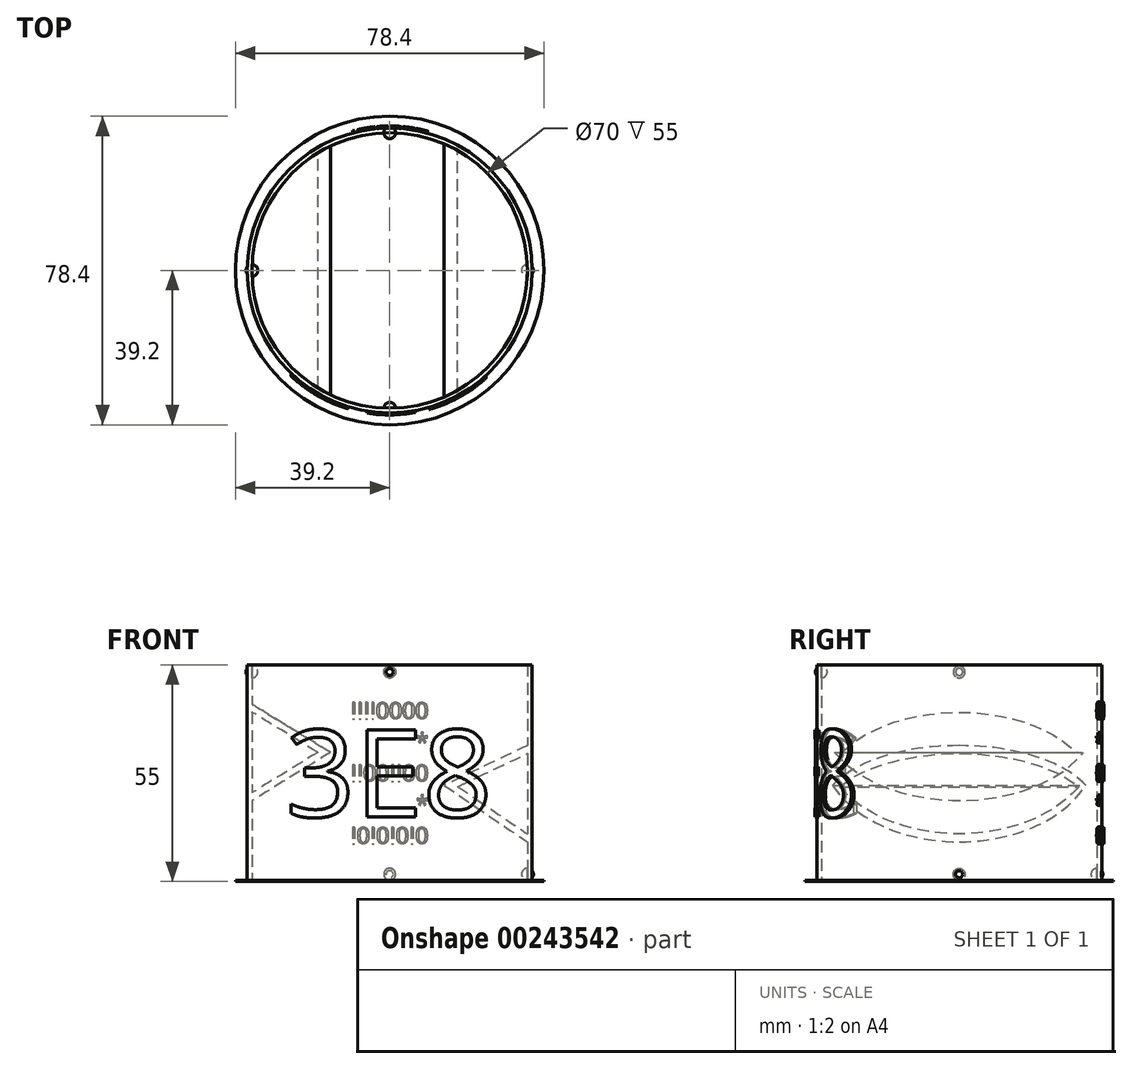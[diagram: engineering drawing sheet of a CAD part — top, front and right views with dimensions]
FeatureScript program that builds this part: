
annotation { "Feature Type Name" : "Feature", "Feature Type Description" : "" }
export const myFeature = defineFeature(function(context is Context, id is Id, definition is map)
    precondition{}
    {
        {
            var Q0;
            Q0=qCreatedBy(makeId("Top.planeOp"),FACE);
            var sketch = newSketch(context, id + "F0", { "sketchPlane" : qUnion([Q0])});
            skCircle(sketch, "E0", {"center": v(0, 0) * mm, "radius": 35 * mm});
            skCircle(sketch, "E1.0", {"center": v(0, 0) * mm, "radius": 36.2 * mm});
            skSolve(sketch);
        }
        {
            var Q0;
            Q0=qSketchRegion(id+"F0",true);
            extrude(context, id + "F1", {"entities" : qUnion([Q0]), "depth" : 55 * mm});
        }
        {
            var Q0;
            Q0=makeQuery(id+"F1.opExtrude","CAP_FACE",FACE,{"disambiguationData":[OSD([sQuery(id+"F0.wireOp",EDGE,"E0"),sQuery(id+"F0.wireOp",EDGE,"E1.0")])],"isStart":false});
            cPlane(context, id + "F2", {"entities" : qUnion([Q0]), "cplaneType" : CPlaneType.OFFSET, "offset" : 4 * mm, "width" : 150 * mm, "height" : 150 * mm});
        }
        {
            var Q0;
            Q0=makeQuery(id+"F1.opExtrude","CAP_FACE",FACE,{"disambiguationData":[OSD([sQuery(id+"F0.wireOp",EDGE,"E0"),sQuery(id+"F0.wireOp",EDGE,"E1.0")])],"isStart":true});
            cPlane(context, id + "F3", {"entities" : qUnion([Q0]), "cplaneType" : CPlaneType.OFFSET, "offset" : 4 * mm, "width" : 150 * mm, "height" : 150 * mm});
        }
        {
            var Q0;
            Q0=makeQuery(id+"F1.opExtrude","CAP_FACE",FACE,{"disambiguationData":[OSD([sQuery(id+"F0.wireOp",EDGE,"E0"),sQuery(id+"F0.wireOp",EDGE,"E1.0")])],"isStart":true});
            cPlane(context, id + "F4", {"entities" : qUnion([Q0]), "cplaneType" : CPlaneType.OFFSET, "offset" : 27.5 * mm, "oppositeDirection" : true, "width" : 150 * mm, "height" : 150 * mm});
        }
        {
            var Q0;
            Q0=qCreatedBy(id+"F2.planeOp",FACE);
            var sketch = newSketch(context, id + "F5", { "sketchPlane" : qUnion([Q0])});
            skCircle(sketch, "E2.0", {"center": v(0, 0) * mm, "radius": 36.2 * mm});
            skSolve(sketch);
        }
        {
            var Q0;
            Q0=makeQuery(id+"F1.opExtrude","CAP_FACE",FACE,{"disambiguationData":[OSD([sQuery(id+"F0.wireOp",EDGE,"E0"),sQuery(id+"F0.wireOp",EDGE,"E1.0")])],"isStart":false});
            extrude(context, id + "F6", {"entities" : qUnion([Q0]), "operationType" : NewBodyOperationType.ADD, "depth" : 2 * mm});
        }
        {
            var Q0;
            Q0=qCreatedBy(id+"F4.planeOp",FACE);
            var sketch = newSketch(context, id + "F7", { "sketchPlane" : qUnion([Q0])});
            skCircle(sketch, "E3.0", {"center": v(0, 0) * mm, "radius": 35 * mm});
            skSolve(sketch);
        }
        {
            var Q0;
            Q0=qSketchRegion(id+"F7",true);
            extrude(context, id + "F8", {"entities" : qUnion([Q0]), "operationType" : NewBodyOperationType.REMOVE, "oppositeDirection" : true, "depth" : 22 * mm, "hasSecondDirection" : true, "secondDirectionOppositeDirection" : false, "secondDirectionDepth" : 22 * mm});
        }
        {
            var Q0;
            Q0=qCreatedBy(makeId("Front.planeOp"),FACE);
            var sketch = newSketch(context, id + "F9", { "sketchPlane" : qUnion([Q0])});
            skLineSegment(sketch, "E4", {"start": v(-35, 0) * mm, "end": v(-35, 55) * mm, "construction": true});
            skLineSegment(sketch, "E5", {"start": v(35, 55) * mm, "end": v(35, 0) * mm, "construction": true});
            skLineSegment(sketch, "E6", {"start": v(-35, 55) * mm, "end": v(-35, 45) * mm, "construction": true});
            skLineSegment(sketch, "E7.0", {"start": v(-35, 55) * mm, "end": v(35, 55) * mm, "construction": true});
            skLineSegment(sketch, "E8", {"start": v(-35, 45) * mm, "end": v(-15, 32.75) * mm});
            skLineSegment(sketch, "E9", {"start": v(-15, 32.75) * mm, "end": v(-35, 20.5) * mm});
            skLineSegment(sketch, "E10", {"start": v(-35, 20.5) * mm, "end": v(-35, 22.5) * mm});
            skLineSegment(sketch, "E11", {"start": v(-35, 22.5) * mm, "end": v(-18.27, 32.75) * mm});
            skLineSegment(sketch, "E12", {"start": v(-18.27, 32.75) * mm, "end": v(-35, 43) * mm});
            skLineSegment(sketch, "E13", {"start": v(-35, 43) * mm, "end": v(-35, 45) * mm});
            skLineSegment(sketch, "E14", {"start": v(-15, 32.75) * mm, "end": v(-35, 32.75) * mm, "construction": true});
            skLineSegment(sketch, "E15", {"start": v(-35, 0) * mm, "end": v(35, 0) * mm, "construction": true});
            skLineSegment(sketch, "E16", {"start": v(35, 0) * mm, "end": v(35, 10) * mm, "construction": true});
            skLineSegment(sketch, "E17", {"start": v(35, 34.5) * mm, "end": v(13.83, 24.4) * mm});
            skLineSegment(sketch, "E18", {"start": v(13.83, 24.4) * mm, "end": v(35, 10) * mm});
            skLineSegment(sketch, "E19", {"start": v(35, 12) * mm, "end": v(17.29, 24.05) * mm});
            skLineSegment(sketch, "E20", {"start": v(17.29, 24.05) * mm, "end": v(35, 32.5) * mm});
            skLineSegment(sketch, "E21", {"start": v(35, 32.5) * mm, "end": v(35, 34.5) * mm});
            skLineSegment(sketch, "E22", {"start": v(35, 12) * mm, "end": v(35, 10) * mm});
            skLineSegment(sketch, "E23", {"start": v(-35, 27.5) * mm, "end": v(35, 27.5) * mm, "construction": true});
            skLineSegment(sketch, "E24", {"start": v(-35, 27.5) * mm, "end": v(-35, 22.5) * mm, "construction": true});
            skLineSegment(sketch, "E25", {"start": v(35, 32.5) * mm, "end": v(35, 27.5) * mm, "construction": true});
            skPoint(sketch, "E26", {"position": v(0, 27.5) * mm});
            skPoint(sketch, "E27", {"position": v(48.42, 25.24) * mm});
            skSolve(sketch);
        }
        {
            var Q0;
            Q0=qSketchRegion(id+"F9",true);
            extrude(context, id + "F10", {"entities" : qUnion([Q0]), "operationType" : NewBodyOperationType.ADD, "endBound" : BoundingType.UP_TO_NEXT, "depth" : 25 * mm, "hasSecondDirection" : true, "secondDirectionBound" : SecondDirectionBoundingType.UP_TO_NEXT, "secondDirectionOppositeDirection" : true, "secondDirectionDepth" : 25 * mm});
        }
        {
            var Q0;
            Q0=qCreatedBy(id+"F3.planeOp",FACE);
            var sketch = newSketch(context, id + "F11", { "sketchPlane" : qUnion([Q0])});
            skCircle(sketch, "E28.0", {"center": v(0, 0) * mm, "radius": 36.2 * mm});
            skSolve(sketch);
        }
        {
            var Q0;
            Q0=qSketchRegion(id+"F11",true);
            extrude(context, id + "F12", {"entities" : qUnion([Q0]), "operationType" : NewBodyOperationType.REMOVE, "oppositeDirection" : true, "depth" : 4 * mm});
        }
        {
            var Q0;
            Q0=makeQuery(id+"F5.imprint","IMPRINT",FACE,{"disambiguationData":[TD([[makeQuery(id+"F5.imprint","IMPRINT",EDGE,{"derivedFrom":sQuery(id+"F5.wireOp",EDGE,"E2.0")}),1.0]])]});
            extrude(context, id + "F13", {"entities" : qUnion([Q0]), "operationType" : NewBodyOperationType.REMOVE, "oppositeDirection" : true, "depth" : 4 * mm});
        }
        {
            var Q0;
            Q0=makeQuery(id+"F12.boolean.opBoolean","MERGE",FACE,{"derivedFrom":[makeQuery(id+"F1.opExtrude","CAP_FACE",FACE,{"disambiguationData":[OSD([sQuery(id+"F0.wireOp",EDGE,"E0"),sQuery(id+"F0.wireOp",EDGE,"E1.0")])],"isStart":true}),makeQuery(id+"F12.opExtrude","CAP_FACE",FACE,{"disambiguationData":[OSD([sQuery(id+"F11.wireOp",EDGE,"E28.0")])],"isStart":false})]});
            var sketch = newSketch(context, id + "F14", { "sketchPlane" : qUnion([Q0])});
            skCircle(sketch, "E29.0", {"center": v(0, 0) * mm, "radius": 36.2 * mm});
            skCircle(sketch, "E30.0", {"center": v(0, 0) * mm, "radius": 39.2 * mm});
            skSolve(sketch);
        }
        {
            var Q0;
            Q0=makeQuery(id+"F14.imprint","IMPRINT",FACE,{"disambiguationData":[TD([[makeQuery(id+"F14.imprint","IMPRINT",EDGE,{"derivedFrom":sQuery(id+"F14.wireOp",EDGE,"E29.0")}),1.0]])]});
            extrude(context, id + "F15", {"entities" : qUnion([Q0]), "operationType" : NewBodyOperationType.ADD, "oppositeDirection" : true, "depth" : .3 * mm});
        }
        {
            var Q0;
            Q0=qCreatedBy(makeId("Front.planeOp"),FACE);
            cPlane(context, id + "F16", {"entities" : qUnion([Q0]), "cplaneType" : CPlaneType.OFFSET, "offset" : 40 * mm, "width" : 150 * mm, "height" : 150 * mm});
        }
        {
            var Q0;
            Q0=qCreatedBy(id+"F16.planeOp",FACE);
            var sketch = newSketch(context, id + "F17", { "sketchPlane" : qUnion([Q0])});
            skLineSegment(sketch, "E31", {"start": v(0, 0) * mm, "end": v(0, 27.5) * mm, "construction": true});
            skText(sketch, "E32", { "text": "3E8", "fontName": "OpenSans-Regular.ttf"});
            const initialGuessF17  = {"E32": [-0.02646, 0.01638, 1, 0, 0.02224]};
            skSetInitialGuess(sketch, initialGuessF17);
            skSolve(sketch);
        }
        {
            var Q0;
            Q0=qSketchRegion(id+"F17",true);
            extrude(context, id + "F18", {"entities" : qUnion([Q0]), "operationType" : NewBodyOperationType.ADD, "endBound" : BoundingType.UP_TO_NEXT, "oppositeDirection" : true, "depth" : 25 * mm});
        }
        {
            var Q0;
            Q0=qCreatedBy(makeId("Front.planeOp"),FACE);
            cPlane(context, id + "F19", {"entities" : qUnion([Q0]), "cplaneType" : CPlaneType.OFFSET, "offset" : 40 * mm, "oppositeDirection" : true, "width" : 150 * mm, "height" : 150 * mm});
        }
        {
            var Q0;
            Q0=qCreatedBy(id+"F19.planeOp",FACE);
            var sketch = newSketch(context, id + "F20", { "sketchPlane" : qUnion([Q0])});
            skLineSegment(sketch, "E33.0", {"start": v(0, 0) * mm, "end": v(0, 27.5) * mm, "construction": true});
            skText(sketch, "E34", { "text": "IIII0000\n           *\nII00II00\n           *\nI0I0I0I0", "fontName": "OpenSans-Regular.ttf"});
            skLineSegment(sketch, "E35", {"start": v(0, 27.5) * mm, "end": v(0, 45.5) * mm, "construction": true});
            const initialGuessF20  = {"E34": [-0.01, 0.0413, 1, 0, 0.0042]};
            skSetInitialGuess(sketch, initialGuessF20);
            skSolve(sketch);
        }
        {
            var Q0;
            Q0=qSketchRegion(id+"F20",true);
            extrude(context, id + "F21", {"entities" : qUnion([Q0]), "operationType" : NewBodyOperationType.ADD, "endBound" : BoundingType.UP_TO_NEXT, "depth" : 25 * mm});
        }
        {
            var Q0;
            Q0=makeQuery(id+"F15.opExtrude","CAP_FACE",FACE,{"disambiguationData":[OSD([sQuery(id+"F14.wireOp",EDGE,"E29.0"),sQuery(id+"F14.wireOp",EDGE,"E30.0")])],"isStart":false});
            var sketch = newSketch(context, id + "F22", { "sketchPlane" : qUnion([Q0])});
            skCircle(sketch, "E36.0", {"center": v(0, 0) * mm, "radius": 36.2 * mm, "construction": true});
            skCircle(sketch, "E37.0", {"center": v(0, 0) * mm, "radius": 36.7 * mm});
            skCircle(sketch, "E38.0", {"center": v(0, 0) * mm, "radius": 56.7 * mm});
            skSolve(sketch);
        }
        {
            var Q0;
            Q0=makeQuery(id+"F22.imprint","IMPRINT",FACE,{"disambiguationData":[TD([[makeQuery(id+"F22.imprint","IMPRINT",EDGE,{"derivedFrom":sQuery(id+"F22.wireOp",EDGE,"E38.0")}),1.0]])]});
            var Q1;
            Q1=makeQuery(id+"F22.imprint","IMPRINT",FACE,{"disambiguationData":[TD([[makeQuery(id+"F22.imprint","IMPRINT",EDGE,{"derivedFrom":sQuery(id+"F22.wireOp",EDGE,"E37.0")}),-1.0]])]});
            extrude(context, id + "F23", {"entities" : qUnion([Q0, Q1]), "operationType" : NewBodyOperationType.REMOVE, "endBound" : BoundingType.THROUGH_ALL, "depth" : 25 * mm});
        }
        {
            var Q0;
            Q0=qCreatedBy(makeId("Front.planeOp"),FACE);
            var sketch = newSketch(context, id + "F24", { "sketchPlane" : qUnion([Q0])});
            skLineSegment(sketch, "E39", {"start": v(-35, 0) * mm, "end": v(-35, 55) * mm, "construction": true});
            skLineSegment(sketch, "E40", {"start": v(35, 55) * mm, "end": v(35, 0) * mm, "construction": true});
            skLineSegment(sketch, "E41", {"start": v(-35, 54.7) * mm, "end": v(-35, 55) * mm, "construction": true});
            skLineSegment(sketch, "E42", {"start": v(-35, 54.7) * mm, "end": v(-35, 51.7) * mm});
            skArc(sketch, "E43", {"start": v(-35, 51.7) * mm, "mid": v(-33.5, 53.2) * mm, "end": v(-35, 54.7) * mm});
            skPoint(sketch, "E44", {"position": v(35, 27.5) * mm});
            skPoint(sketch, "E45", {"position": v(-35, 27.5) * mm});
            skLineSegment(sketch, "E46", {"start": v(-35, 27.5) * mm, "end": v(35, 27.5) * mm, "construction": true});
            skLineSegment(sketch, "E47", {"start": v(0, 27.5) * mm, "end": v(0, 55) * mm, "construction": true});
            skArc(sketch, "E48.MirrorCS", {"start": v(35, 51.7) * mm, "mid": v(33.5, 53.2) * mm, "end": v(35, 54.7) * mm});
            skLineSegment(sketch, "E49.MirrorCS", {"start": v(35, 54.7) * mm, "end": v(35, 51.7) * mm});
            skArc(sketch, "E50.MirrorCS", {"start": v(35, 3.3) * mm, "mid": v(33.5, 1.8) * mm, "end": v(35, 0.3) * mm});
            skLineSegment(sketch, "E51.MirrorCS", {"start": v(35, 0.3) * mm, "end": v(35, 3.3) * mm});
            skArc(sketch, "E52.MirrorCS", {"start": v(-35, 3.3) * mm, "mid": v(-33.5, 1.8) * mm, "end": v(-35, 0.3) * mm});
            skLineSegment(sketch, "E53.MirrorCS", {"start": v(-35, 0.3) * mm, "end": v(-35, 3.3) * mm});
            skLineSegment(sketch, "E54", {"start": v(-35, 0) * mm, "end": v(35, 0) * mm, "construction": true});
            skSolve(sketch);
        }
        {
            var Q0;
            Q0=makeQuery(id+"F24.imprint","IMPRINT",FACE,{"disambiguationData":[TD([[makeQuery(id+"F24.imprint","IMPRINT",EDGE,{"derivedFrom":sQuery(id+"F24.wireOp",EDGE,"E42")}),1.0]])]});
            var Q1;
            Q1=makeQuery(id+"F24.imprint","IMPRINT",FACE,{"disambiguationData":[TD([[makeQuery(id+"F24.imprint","IMPRINT",EDGE,{"derivedFrom":sQuery(id+"F24.wireOp",EDGE,"E52.MirrorCS")}),-1.0]])]});
            var Q2;
            Q2=sQuery(id+"F24.wireOp",EDGE,"E39");
            revolve(context, id + "F25", {"operationType" : NewBodyOperationType.ADD, "entities" : qUnion([Q0, Q1]), "axis" : qUnion([Q2]), "revolveType" : RevolveType.FULL});
        }
        {
            var Q0;
            Q0=makeQuery(id+"F24.imprint","IMPRINT",FACE,{"disambiguationData":[TD([[makeQuery(id+"F24.imprint","IMPRINT",EDGE,{"derivedFrom":sQuery(id+"F24.wireOp",EDGE,"E48.MirrorCS")}),-1.0]])]});
            var Q1;
            Q1=makeQuery(id+"F24.imprint","IMPRINT",FACE,{"disambiguationData":[TD([[makeQuery(id+"F24.imprint","IMPRINT",EDGE,{"derivedFrom":sQuery(id+"F24.wireOp",EDGE,"E50.MirrorCS")}),1.0]])]});
            var Q2;
            Q2=sQuery(id+"F24.wireOp",EDGE,"E40");
            revolve(context, id + "F26", {"operationType" : NewBodyOperationType.ADD, "entities" : qUnion([Q0, Q1]), "axis" : qUnion([Q2]), "revolveType" : RevolveType.FULL});
        }
        {
            var Q0;
            Q0=qCreatedBy(makeId("Right.planeOp"),FACE);
            var sketch = newSketch(context, id + "F27", { "sketchPlane" : qUnion([Q0])});
            skLineSegment(sketch, "E55", {"start": v(-35, 0) * mm, "end": v(-35, 55) * mm, "construction": true});
            skLineSegment(sketch, "E56", {"start": v(35, 55) * mm, "end": v(35, 0) * mm, "construction": true});
            skLineSegment(sketch, "E57", {"start": v(-35, 54.7) * mm, "end": v(-35, 55) * mm, "construction": true});
            skLineSegment(sketch, "E58", {"start": v(-35, 54.7) * mm, "end": v(-35, 51.7) * mm});
            skArc(sketch, "E59", {"start": v(-35, 51.7) * mm, "mid": v(-33.5, 53.2) * mm, "end": v(-35, 54.7) * mm});
            skPoint(sketch, "E60", {"position": v(35, 27.5) * mm});
            skPoint(sketch, "E61", {"position": v(-35, 27.5) * mm});
            skLineSegment(sketch, "E62", {"start": v(-35, 27.5) * mm, "end": v(35, 27.5) * mm, "construction": true});
            skLineSegment(sketch, "E63", {"start": v(0, 27.5) * mm, "end": v(0, 55) * mm, "construction": true});
            skArc(sketch, "E64.MirrorCS", {"start": v(35, 51.7) * mm, "mid": v(33.5, 53.2) * mm, "end": v(35, 54.7) * mm});
            skLineSegment(sketch, "E65.MirrorCS", {"start": v(35, 54.7) * mm, "end": v(35, 51.7) * mm});
            skArc(sketch, "E66.MirrorCS", {"start": v(35, 3.3) * mm, "mid": v(33.5, 1.8) * mm, "end": v(35, 0.3) * mm});
            skLineSegment(sketch, "E67.MirrorCS", {"start": v(35, 0.3) * mm, "end": v(35, 3.3) * mm});
            skArc(sketch, "E68.MirrorCS", {"start": v(-35, 3.3) * mm, "mid": v(-33.5, 1.8) * mm, "end": v(-35, 0.3) * mm});
            skLineSegment(sketch, "E69.MirrorCS", {"start": v(-35, 0.3) * mm, "end": v(-35, 3.3) * mm});
            skLineSegment(sketch, "E70", {"start": v(-35, 0) * mm, "end": v(35, 0) * mm, "construction": true});
            skSolve(sketch);
        }
        {
            var Q0;
            Q0=makeQuery(id+"F27.imprint","IMPRINT",FACE,{"disambiguationData":[TD([[makeQuery(id+"F27.imprint","IMPRINT",EDGE,{"derivedFrom":sQuery(id+"F27.wireOp",EDGE,"E58")}),1.0]])]});
            var Q1;
            Q1=makeQuery(id+"F27.imprint","IMPRINT",FACE,{"disambiguationData":[TD([[makeQuery(id+"F27.imprint","IMPRINT",EDGE,{"derivedFrom":sQuery(id+"F27.wireOp",EDGE,"E68.MirrorCS")}),-1.0]])]});
            var Q2;
            Q2=sQuery(id+"F27.wireOp",EDGE,"E55");
            revolve(context, id + "F28", {"operationType" : NewBodyOperationType.ADD, "entities" : qUnion([Q0, Q1]), "axis" : qUnion([Q2]), "revolveType" : RevolveType.FULL});
        }
        {
            var Q0;
            Q0=makeQuery(id+"F27.imprint","IMPRINT",FACE,{"disambiguationData":[TD([[makeQuery(id+"F27.imprint","IMPRINT",EDGE,{"derivedFrom":sQuery(id+"F27.wireOp",EDGE,"E66.MirrorCS")}),1.0]])]});
            var Q1;
            Q1=makeQuery(id+"F27.imprint","IMPRINT",FACE,{"disambiguationData":[TD([[makeQuery(id+"F27.imprint","IMPRINT",EDGE,{"derivedFrom":sQuery(id+"F27.wireOp",EDGE,"E64.MirrorCS")}),-1.0]])]});
            var Q2;
            Q2=sQuery(id+"F27.wireOp",EDGE,"E56");
            revolve(context, id + "F29", {"operationType" : NewBodyOperationType.ADD, "entities" : qUnion([Q0, Q1]), "axis" : qUnion([Q2]), "revolveType" : RevolveType.FULL});
        }
    });
